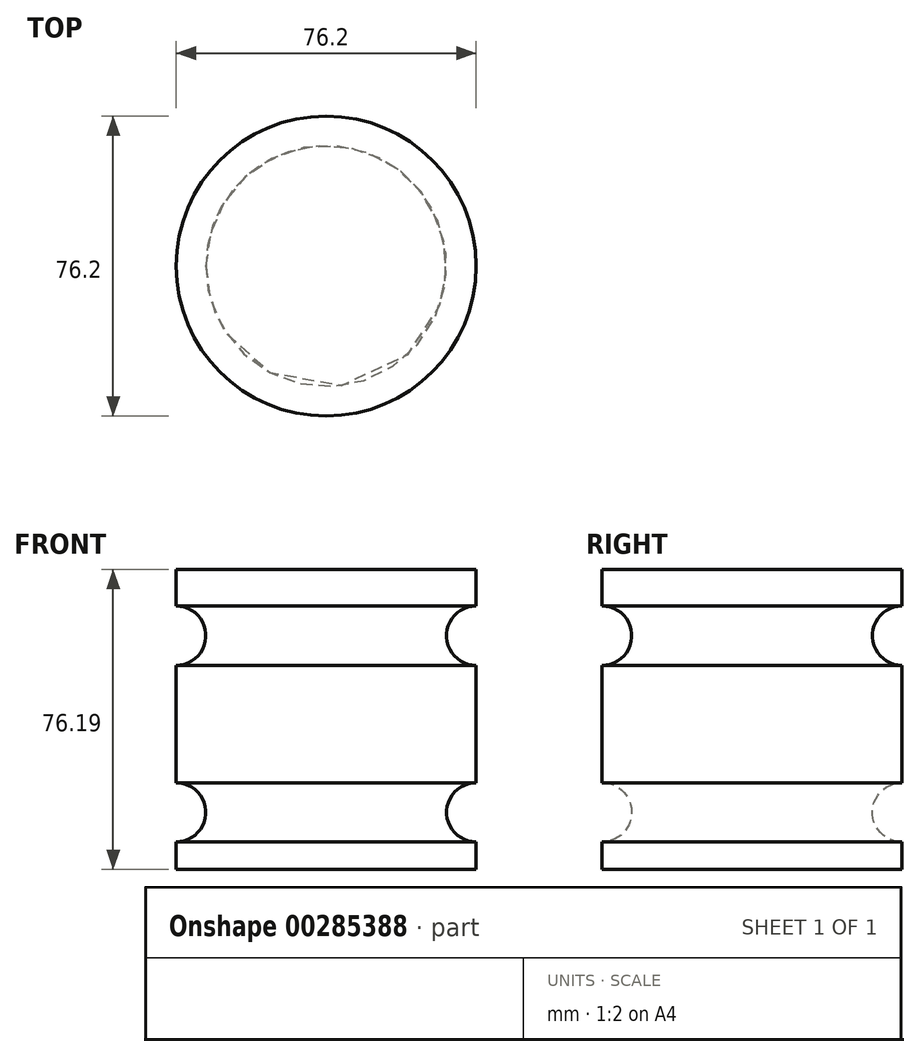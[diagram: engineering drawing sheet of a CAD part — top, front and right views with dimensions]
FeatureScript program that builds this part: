
annotation { "Feature Type Name" : "Feature", "Feature Type Description" : "" }
export const myFeature = defineFeature(function(context is Context, id is Id, definition is map)
    precondition{}
    {
        {
            var Q0;
            Q0=qCreatedBy(makeId("Front.planeOp"),FACE);
            var sketch = newSketch(context, id + "F0", { "sketchPlane" : qUnion([Q0])});
            skLineSegment(sketch, "E0.bottom", {"start": v(0, 0) * mm, "end": v(-38.1, 0) * mm});
            skLineSegment(sketch, "E0.top", {"start": v(0, 76.2) * mm, "end": v(-38.1, 76.2) * mm});
            skLineSegment(sketch, "E0.left", {"start": v(0, 0) * mm, "end": v(0, 7) * mm});
            skLineSegment(sketch, "E0.right", {"start": v(-38.1, 0) * mm, "end": v(-38.1, 76.2) * mm});
            skArc(sketch, "E1", {"start": v(0, 22.02) * mm, "mid": v(-7.5, 14.51) * mm, "end": v(0, 7) * mm});
            skArc(sketch, "E2", {"start": v(0, 66.92) * mm, "mid": v(-7.53, 59.39) * mm, "end": v(0, 51.85) * mm});
            skLineSegment(sketch, "E3.trimOffspring", {"start": v(0, 22.02) * mm, "end": v(0, 51.85) * mm});
            skLineSegment(sketch, "E4.trimOffspring", {"start": v(0, 66.92) * mm, "end": v(0, 76.2) * mm});
            skSolve(sketch);
        }
        {
            var Q0;
            Q0=makeQuery(id+"F0.imprint","IMPRINT",FACE,{"disambiguationData":[TD([[makeQuery(id+"F0.imprint","IMPRINT",EDGE,{"derivedFrom":sQuery(id+"F0.wireOp",EDGE,"E0.bottom")}),-1.0]])]});
            var Q1;
            Q1=sQuery(id+"F0.wireOp",EDGE,"E0.right");
            revolve(context, id + "F1", {"entities" : qUnion([Q0]), "axis" : qUnion([Q1]), "revolveType" : RevolveType.FULL});
        }
    });
